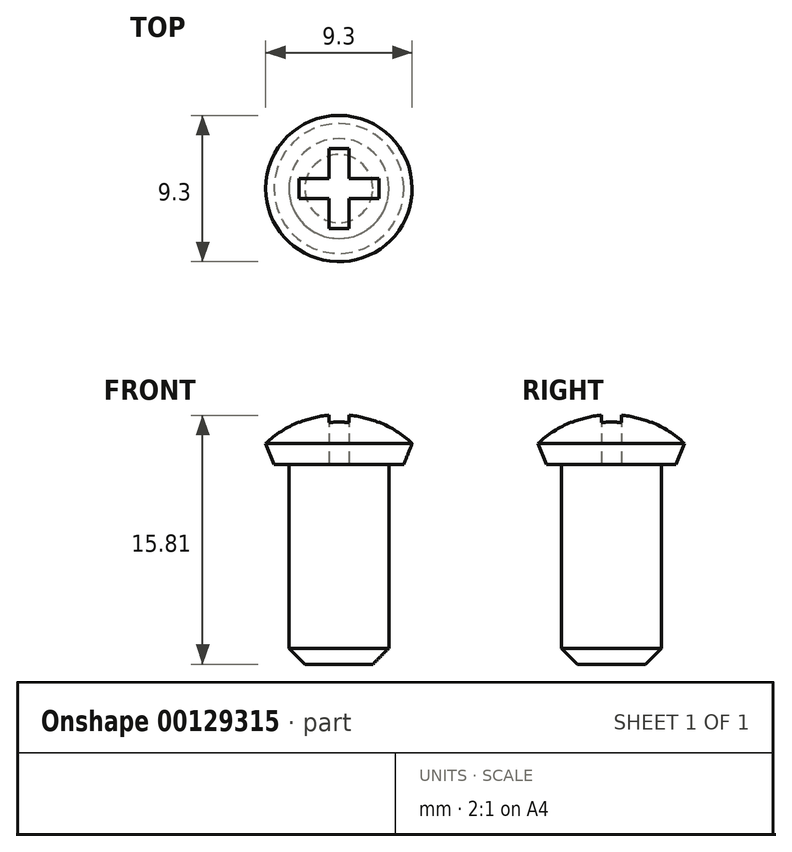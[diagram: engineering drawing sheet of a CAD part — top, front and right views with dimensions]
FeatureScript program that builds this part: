
annotation { "Feature Type Name" : "Feature", "Feature Type Description" : "" }
export const myFeature = defineFeature(function(context is Context, id is Id, definition is map)
    precondition{}
    {
        {
            var Q0;
            Q0=qCreatedBy(makeId("Front.planeOp"),FACE);
            var sketch = newSketch(context, id + "F0", { "sketchPlane" : qUnion([Q0])});
            skLineSegment(sketch, "E0", {"start": v(5.71, 0) * mm, "end": v(3.17, 0) * mm});
            skLineSegment(sketch, "E1", {"start": v(3.17, 0) * mm, "end": v(3.18, -12.7) * mm});
            skLineSegment(sketch, "E2", {"start": v(3.18, -12.7) * mm, "end": v(0, -12.7) * mm});
            skLineSegment(sketch, "E3", {"start": v(0, -12.7) * mm, "end": v(0, 3.18) * mm});
            skArc(sketch, "E4", {"start": v(5.72, 0) * mm, "mid": v(3.27, 2.33) * mm, "end": v(0, 3.18) * mm});
            skLineSegment(sketch, "E5", {"start": v(0, -12.7) * mm, "end": v(0, -23.97) * mm, "construction": true});
            skSolve(sketch);
        }
        {
            var Q0;
            Q0=makeQuery(id+"F0.imprint","IMPRINT",FACE,{"disambiguationData":[TD([[makeQuery(id+"F0.imprint","IMPRINT",EDGE,{"derivedFrom":sQuery(id+"F0.wireOp",EDGE,"E0")}),-1.0]])]});
            var Q1;
            Q1=sQuery(id+"F0.wireOp",EDGE,"E3");
            revolve(context, id + "F1", {"entities" : qUnion([Q0]), "axis" : qUnion([Q1]), "revolveType" : RevolveType.FULL});
        }
        {
            var Q0;
            Q0=makeQuery(id+"F1.opRevolve","SWEPT_EDGE",EDGE,{"disambiguationData":[OSD([sQuery(id+"F0.wireOp",EDGE,"E0"),sQuery(id+"F0.wireOp",EDGE,"E4")])]});
            chamfer(context, id + "F2", {"entities" : qUnion([Q0]), "width" : 0.76 * mm, "tangentPropagation" : true});
        }
        {
            var Q0;
            Q0=qCreatedBy(makeId("Top.planeOp"),FACE);
            var sketch = newSketch(context, id + "F3", { "sketchPlane" : qUnion([Q0])});
            skLineSegment(sketch, "E6", {"start": v(-6.83, 0) * mm, "end": v(6.52, 0) * mm, "construction": true});
            skLineSegment(sketch, "E7", {"start": v(0, 5.39) * mm, "end": v(0, -6.35) * mm, "construction": true});
            skLineSegment(sketch, "E8.bottom", {"start": v(-0.64, 2.54) * mm, "end": v(0.63, 2.54) * mm});
            skLineSegment(sketch, "E8.top", {"start": v(-0.63, -2.54) * mm, "end": v(0.63, -2.54) * mm});
            skLineSegment(sketch, "E8.left", {"start": v(-0.64, 2.54) * mm, "end": v(-0.64, 0.63) * mm});
            skLineSegment(sketch, "E8.right", {"start": v(0.64, 2.54) * mm, "end": v(0.64, 0.63) * mm});
            skLineSegment(sketch, "E9.bottom", {"start": v(-2.54, 0.64) * mm, "end": v(-0.64, 0.64) * mm});
            skLineSegment(sketch, "E9.top", {"start": v(-2.54, -0.63) * mm, "end": v(-0.64, -0.63) * mm});
            skLineSegment(sketch, "E9.left", {"start": v(-2.54, 0.63) * mm, "end": v(-2.54, -0.63) * mm});
            skLineSegment(sketch, "E9.right", {"start": v(2.54, 0.64) * mm, "end": v(2.54, -0.63) * mm});
            skLineSegment(sketch, "E10.trimOffspring", {"start": v(0.63, 0.64) * mm, "end": v(2.54, 0.64) * mm});
            skLineSegment(sketch, "E11.trimOffspring", {"start": v(0.64, -0.63) * mm, "end": v(0.64, -2.54) * mm});
            skLineSegment(sketch, "E12.trimOffspring", {"start": v(-0.64, -0.63) * mm, "end": v(-0.64, -2.54) * mm});
            skLineSegment(sketch, "E13.trimOffspring", {"start": v(0.64, -0.63) * mm, "end": v(2.54, -0.63) * mm});
            skSolve(sketch);
        }
        {
            var Q0;
            Q0 = qSketchRegion(id + "F3", true);
            extrude(context, id + "F4", {"entities" : qUnion([Q0]), "operationType" : NewBodyOperationType.REMOVE, "endBound" : BoundingType.THROUGH_ALL, "depth" : 25.4 * mm});
        }
        {
            var Q0;
            Q0=makeQuery(id+"F1.opRevolve","SWEPT_EDGE",EDGE,{"disambiguationData":[OSD([sQuery(id+"F0.wireOp",EDGE,"E1"),sQuery(id+"F0.wireOp",EDGE,"E2")])]});
            chamfer(context, id + "F5", {"entities" : qUnion([Q0]), "width" : 1.02 * mm, "tangentPropagation" : true});
        }
    });
